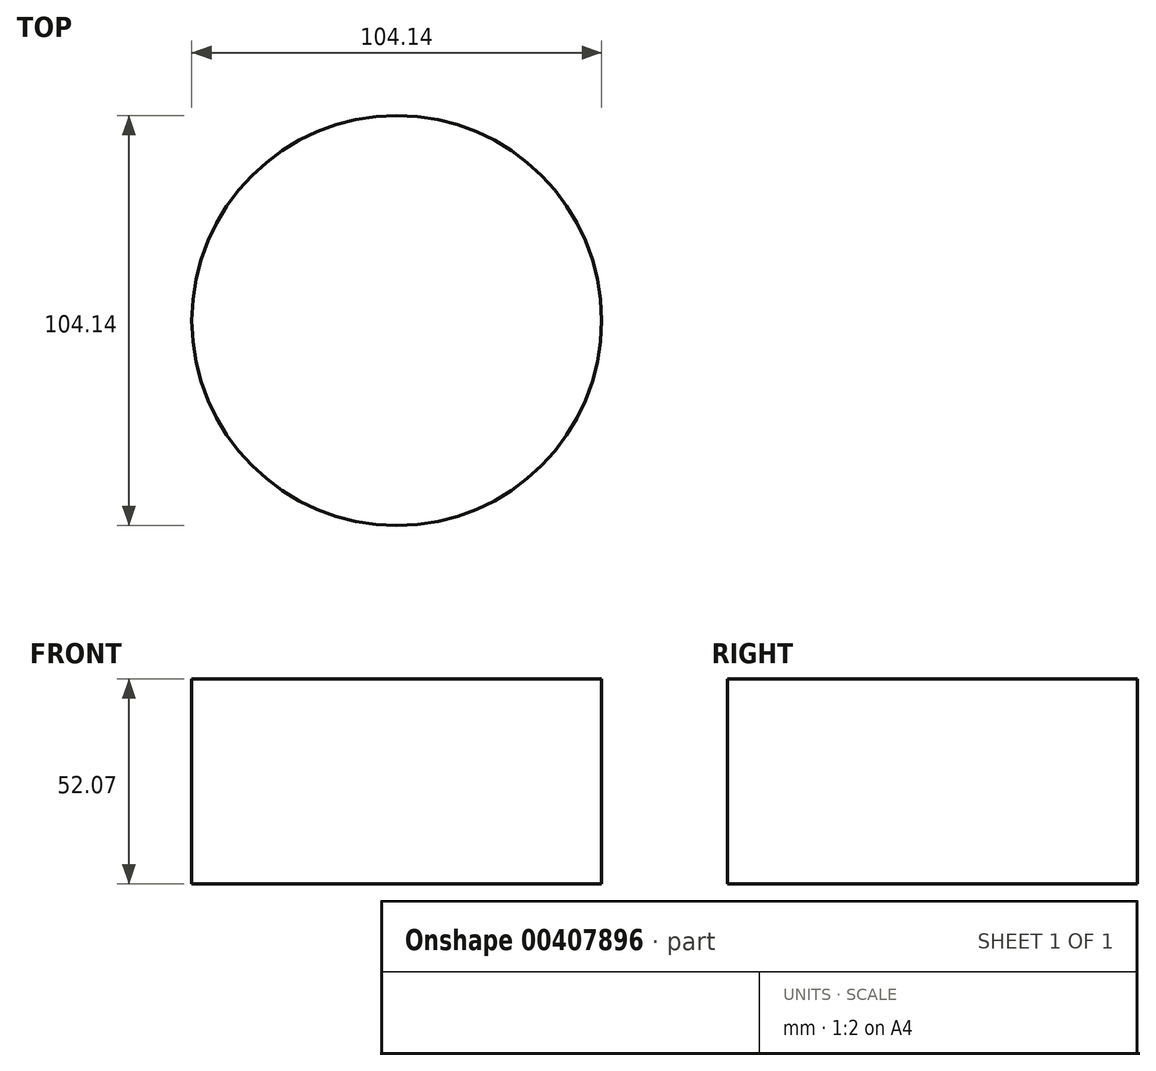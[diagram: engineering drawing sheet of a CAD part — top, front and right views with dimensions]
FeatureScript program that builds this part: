
annotation { "Feature Type Name" : "Feature", "Feature Type Description" : "" }
export const myFeature = defineFeature(function(context is Context, id is Id, definition is map)
    precondition{}
    {
        {
            var Q0;
            Q0=qCreatedBy(makeId("Front.planeOp"),FACE);
            var sketch = newSketch(context, id + "F0", { "sketchPlane" : qUnion([Q0])});
            skLineSegment(sketch, "E0.bottom", {"start": v(0, 0) * mm, "end": v(52.07, 0) * mm});
            skLineSegment(sketch, "E0.top", {"start": v(0, 52.07) * mm, "end": v(52.07, 52.07) * mm});
            skLineSegment(sketch, "E0.left", {"start": v(0, 0) * mm, "end": v(0, 52.07) * mm});
            skLineSegment(sketch, "E0.right", {"start": v(52.07, 0) * mm, "end": v(52.07, 52.07) * mm});
            skSolve(sketch);
        }
        {
            var Q0;
            Q0 = qSketchRegion(id + "F0", true);
            var Q1;
            Q1=sQuery(id+"F0.wireOp",EDGE,"E0.left");
            revolve(context, id + "F1", {"entities" : qUnion([Q0]), "axis" : qUnion([Q1]), "revolveType" : RevolveType.FULL});
        }
    });
